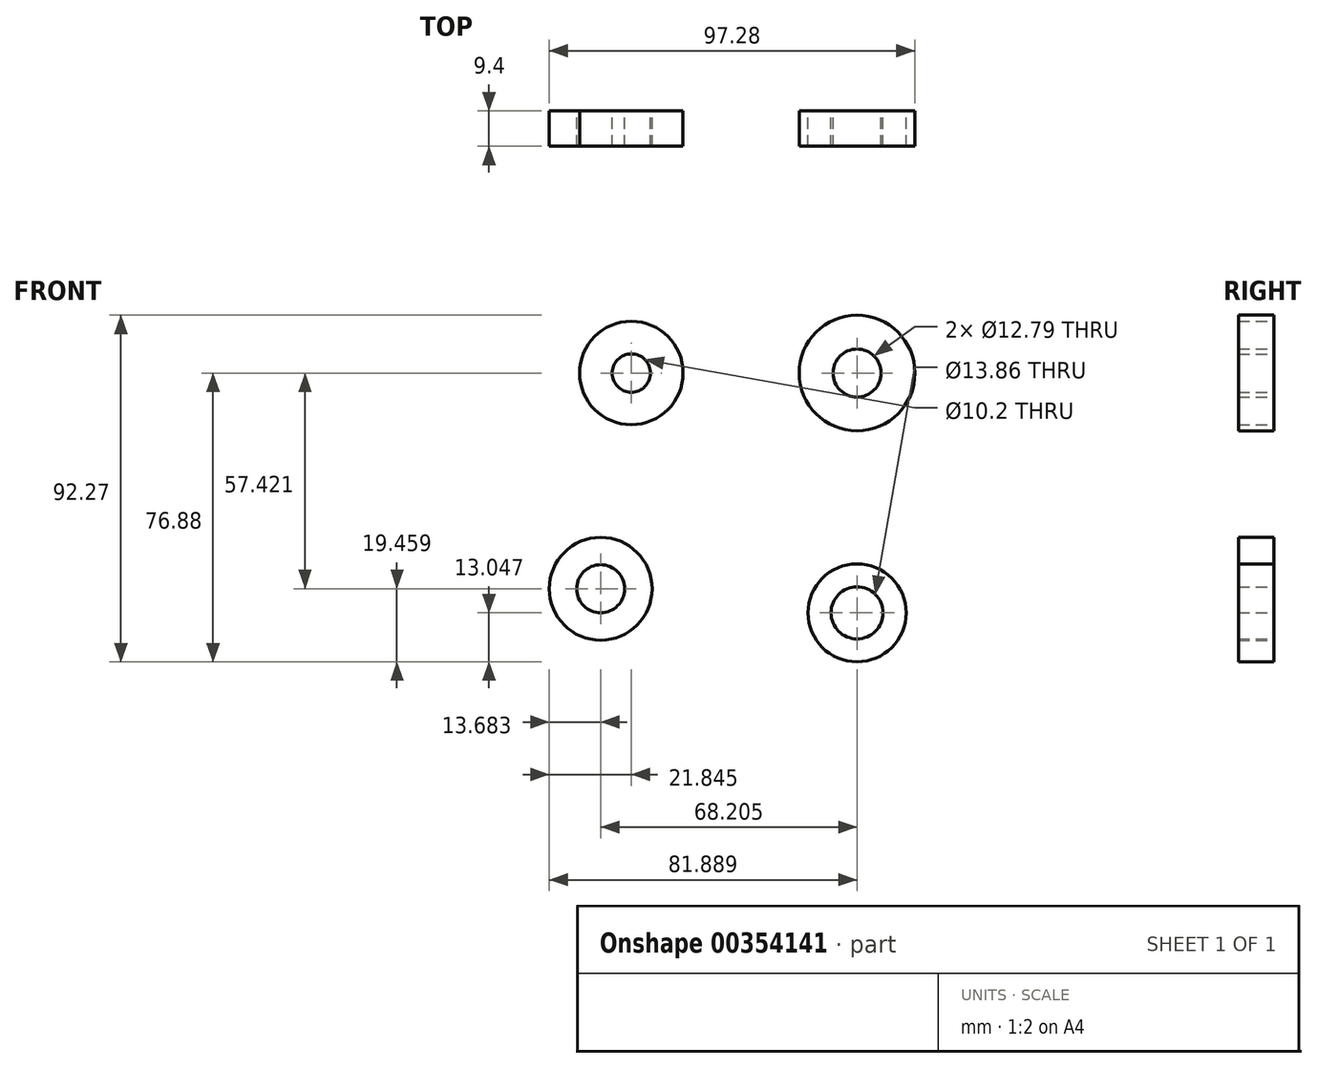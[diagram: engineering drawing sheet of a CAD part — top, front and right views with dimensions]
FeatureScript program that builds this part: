
annotation { "Feature Type Name" : "Feature", "Feature Type Description" : "" }
export const myFeature = defineFeature(function(context is Context, id is Id, definition is map)
    precondition{}
    {
        {
            var Q0;
            Q0=qCreatedBy(makeId("Front.planeOp"),FACE);
            var sketch = newSketch(context, id + "F0", { "sketchPlane" : qUnion([Q0])});
            skCircle(sketch, "E0", {"center": v(-32.65, 34.54) * mm, "radius": 13.76 * mm});
            skCircle(sketch, "E1", {"center": v(-32.65, 34.54) * mm, "radius": 5.1 * mm});
            skCircle(sketch, "E2", {"center": v(27.4, 34.54) * mm, "radius": 15.4 * mm});
            skCircle(sketch, "E3", {"center": v(27.4, 34.54) * mm, "radius": 6.4 * mm});
            skCircle(sketch, "E4", {"center": v(-40.8, -22.88) * mm, "radius": 13.69 * mm});
            skCircle(sketch, "E5", {"center": v(-40.8, -22.88) * mm, "radius": 6.4 * mm});
            skCircle(sketch, "E6", {"center": v(27.4, -29.3) * mm, "radius": 13.05 * mm});
            skCircle(sketch, "E7", {"center": v(27.4, -29.3) * mm, "radius": 6.93 * mm});
            skSolve(sketch);
        }
        {
            var Q0;
            Q0 = qSketchRegion(id + "F0", true);
            extrude(context, id + "F1", {"entities" : qUnion([Q0]), "depth" : 9.4 * mm});
        }
    });
